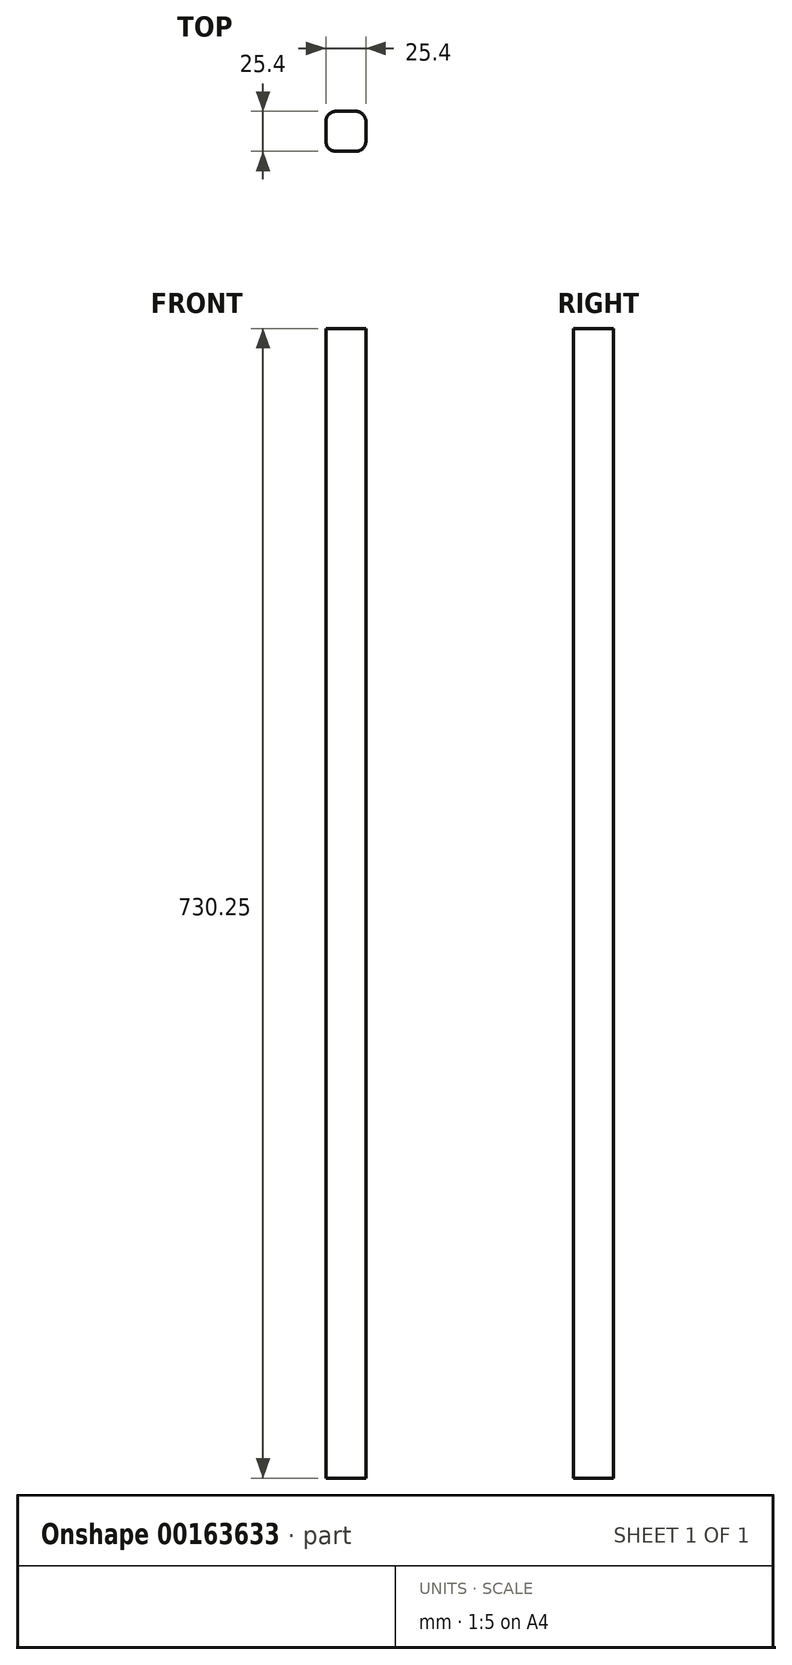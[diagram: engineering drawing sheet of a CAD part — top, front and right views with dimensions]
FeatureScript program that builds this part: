
annotation { "Feature Type Name" : "Feature", "Feature Type Description" : "" }
export const myFeature = defineFeature(function(context is Context, id is Id, definition is map)
    precondition{}
    {
        {
            var Q0;
            Q0=qCreatedBy(makeId("Top.planeOp"),FACE);
            var sketch = newSketch(context, id + "F0", { "sketchPlane" : qUnion([Q0])});
            skLineSegment(sketch, "E0.bottom", {"start": v(6.35, 12.7) * mm, "end": v(-6.35, 12.7) * mm});
            skLineSegment(sketch, "E0.top", {"start": v(6.35, -12.7) * mm, "end": v(-6.35, -12.7) * mm});
            skLineSegment(sketch, "E0.left", {"start": v(12.7, 6.35) * mm, "end": v(12.7, -6.35) * mm});
            skLineSegment(sketch, "E0.right", {"start": v(-12.7, 6.35) * mm, "end": v(-12.7, -6.35) * mm});
            skPoint(sketch, "E0.middle", {"position": v(0, 0) * mm});
            skPoint(sketch, "E1.visualSharp", {"position": v(-12.7, 12.7) * mm});
            skArc(sketch, "E1.filletArc", {"start": v(-6.35, 12.7) * mm, "mid": v(-10.84, 10.84) * mm, "end": v(-12.7, 6.35) * mm});
            skPoint(sketch, "E2.visualSharp", {"position": v(-12.7, -12.7) * mm});
            skArc(sketch, "E2.filletArc", {"start": v(-12.7, -6.35) * mm, "mid": v(-10.84, -10.84) * mm, "end": v(-6.35, -12.7) * mm});
            skPoint(sketch, "E3.visualSharp", {"position": v(12.7, -12.7) * mm});
            skArc(sketch, "E3.filletArc", {"start": v(6.35, -12.7) * mm, "mid": v(10.84, -10.84) * mm, "end": v(12.7, -6.35) * mm});
            skPoint(sketch, "E4.visualSharp", {"position": v(12.7, 12.7) * mm});
            skArc(sketch, "E4.filletArc", {"start": v(12.7, 6.35) * mm, "mid": v(10.84, 10.84) * mm, "end": v(6.35, 12.7) * mm});
            skSolve(sketch);
        }
        {
            var Q0;
            Q0=qSketchRegion(id+"F0",true);
            extrude(context, id + "F1", {"entities" : qUnion([Q0]), "depth" : 730.25 * mm, "offsetDistance" : 25.4 * mm});
        }
    });
